# Revit family: Алсель_Затвор_Дисковый_Механический_Редуктор
name_source: partatom
category: Арматура трубопроводов
revit_build: Autodesk Revit 2016 (Build: 20150714_1515(x64)
units: mm (PartAtom-declared; Revit-internal decimal feet)

## family parameters
Всегда вертикально = Да
На основе рабочей плоскости = Нет
Общий = Нет
При загрузке вырезать с полостями = Нет
Размер круглого соединителя = Использовать диаметр
Тип детали = Вставляется

## types (7) — shared parameters
ADSK_URL страницы изделия = http://www.ahlsell.ru
ADSK_Единица измерения = шт.
ADSK_Завод-изготовитель = Алсель
ADSK_Примечание = Механический редуктор
ADSK_Страна производства = AHLSELL_Запорная арматура – Россия, Китай
H_кв = 9 мм
Давление = 16.0 Па
Закрытое_Положение = Да
Открытое_Положение = Нет
Рукоятка толщина = 15.8 мм
Скругление ушей = 10 мм
СтенкаРучки = 10 мм
УшиВысота = 70 мм
УшиШирина = 40 мм

## per-type parameters (varying)
| type | ADSK_Код изделия | ADSK_Масса_Текст | A_ВерхняяПривязка | B_НижняяПривязка | D1_ДиаметрДиска | D1_Наружний | D2_ДиметрНаружний | D3_ОтверстияПроушин | D4_ВнутреннийДиаметрРукоятки | D4_НаружнийДиаметрРукоятка | DN | DY | E_СдвигРучки | F_СдвигКолеса | R1 | R4_РучкиВнутренний | РазмерРедуктора | С_Ширина | С_ушей | УголАльфа |
| Затвор "бабочка" дисковый хромированный чугунный DN 200 | AHLBV200R |  | 268 мм | 177 мм | 202.5 мм | 232.5 мм | 295 мм | 23 мм | 250 мм | 270 мм | 200 мм | 200 мм | 206 мм | 63 мм | 101.3 мм | 125 мм | 80 мм | 60 мм | 50 мм | 30.00° |
| Затвор "бабочка" дисковый хромированный чугунный DN 250 | AHLBV250 | 26.8 | 312 мм | 210 мм | 250.4 мм | 280.4 мм | 355 мм | 28 мм | 250 мм | 270 мм | 250 мм | 250 мм | 206 мм | 63 мм | 125.2 мм | 125 мм | 80 мм | 68 мм | 55 мм | 30.00° |
| Затвор "бабочка" дисковый хромированный чугунный DN 300 | AHLBV300 | 40 | 339 мм | 242 мм | 301.6 мм | 331.6 мм | 410 мм | 28 мм | 250 мм | 270 мм | 300 мм | 300 мм | 206 мм | 75 мм | 150.8 мм | 125 мм | 90 мм | 78 мм | 65 мм | 30.00° |
| Затвор "бабочка" дисковый хромированный чугунный DN 350 | AHLBV350 | 56 | 407 мм | 267 мм | 333.5 мм | 363.5 мм | 470 мм | 28 мм | 250 мм | 270 мм | 350 мм | 350 мм | 206 мм | 75 мм | 166.8 мм | 125 мм | 90 мм | 78 мм | 65 мм | 22.50° |
| Затвор "бабочка" дисковый хромированный чугунный DN 400 | AHLBV400 | 96 | 455 мм | 309 мм | 389.7 мм | 419.7 мм | 525 мм | 31 мм | 365 мм | 385 мм | 400 мм | 400 мм | 250 мм | 115 мм | 194.9 мм | 182.5 мм | 130 мм | 102 мм | 95 мм | 22.50° |
| Затвор "бабочка" дисковый хромированный чугунный DN 450 | AHLBV450 | 122 | 477 мм | 328 мм | 440.5 мм | 470.5 мм | 585 мм | 31 мм | 365 мм | 385 мм | 450 мм | 450 мм | 250 мм | 115 мм | 220.3 мм | 182.5 мм | 130 мм | 114 мм | 100 мм | 22.50° |
| Затвор "бабочка" дисковый хромированный чугунный DN 500 | AHLBV500 | 202 | 603 мм | 361 мм | 491.6 мм | 521.6 мм | 650 мм | 34 мм | 250 мм | 270 мм | 500 мм | 500 мм | 260 мм | 165 мм | 245.8 мм | 125 мм | 180 мм | 127 мм | 120 мм | 18.00° |

note: column(s) folded — value = type name in every type: ADSK_Наименование
